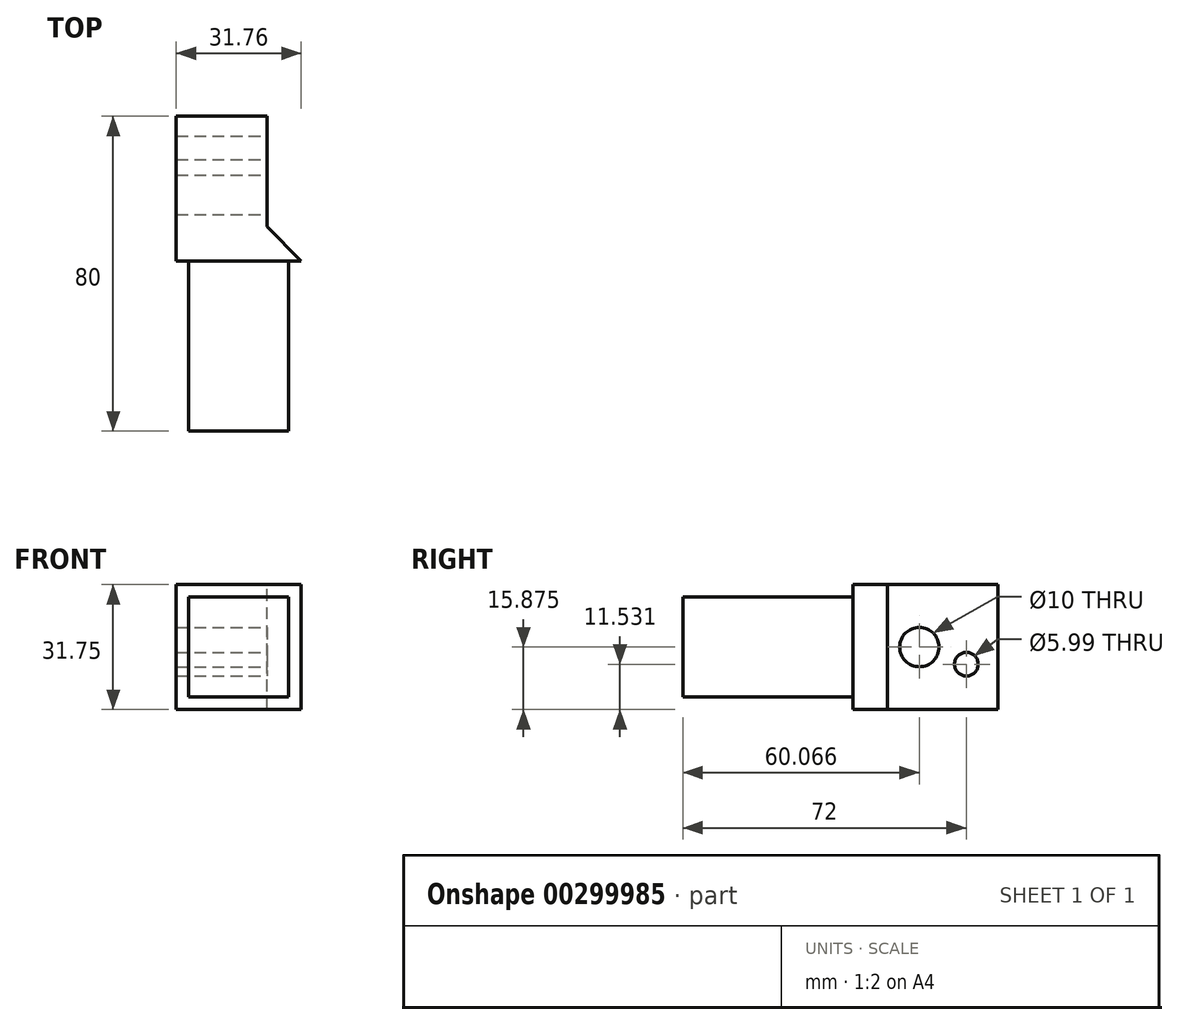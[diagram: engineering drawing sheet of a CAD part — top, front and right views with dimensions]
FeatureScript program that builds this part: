
annotation { "Feature Type Name" : "Feature", "Feature Type Description" : "" }
export const myFeature = defineFeature(function(context is Context, id is Id, definition is map)
    precondition{}
    {
        {
            var Q0;
            Q0=qCreatedBy(makeId("Top.planeOp"),FACE);
            var sketch = newSketch(context, id + "F0", { "sketchPlane" : qUnion([Q0])});
            skLineSegment(sketch, "E0.bottom", {"start": v(-15.88, 40) * mm, "end": v(15.88, 40) * mm});
            skLineSegment(sketch, "E0.top", {"start": v(-15.88, -40) * mm, "end": v(15.88, -40) * mm});
            skLineSegment(sketch, "E0.left", {"start": v(-15.88, 40) * mm, "end": v(-15.88, -40) * mm});
            skLineSegment(sketch, "E0.right", {"start": v(15.88, 40) * mm, "end": v(15.88, -40) * mm});
            skSolve(sketch);
        }
        {
            var Q0;
            Q0=qSketchRegion(id+"F0",true);
            extrude(context, id + "F1", {"entities" : qUnion([Q0]), "depth" : 31.75 * mm, "offsetDistance" : 25 * mm});
        }
        {
            var Q0;
            Q0=makeQuery(id+"F1.opExtrude","SWEPT_FACE",FACE,{"disambiguationData":[OSD([sQuery(id+"F0.wireOp",EDGE,"E0.right")])]});
            var sketch = newSketch(context, id + "F2", { "sketchPlane" : qUnion([Q0])});
            skCircle(sketch, "E1", {"center": v(20.07, 15.88) * mm, "radius": 5 * mm});
            skLineSegment(sketch, "E2", {"start": v(20.07, 15.88) * mm, "end": v(26.86, 15.88) * mm});
            skCircle(sketch, "E3", {"center": v(32, 11.53) * mm, "radius": 3 * mm});
            skLineSegment(sketch, "E4", {"start": v(32, 11.53) * mm, "end": v(20.07, 15.88) * mm});
            skSolve(sketch);
        }
        {
            var Q0;
            Q0=qSketchRegion(id+"F2",true);
            extrude(context, id + "F3", {"entities" : qUnion([Q0]), "operationType" : NewBodyOperationType.REMOVE, "endBound" : BoundingType.THROUGH_ALL, "oppositeDirection" : true, "depth" : 25 * mm, "offsetDistance" : 25 * mm});
        }
        {
            var Q0;
            Q0=makeQuery(id+"F1.opExtrude","CAP_FACE",FACE,{"disambiguationData":[OSD([sQuery(id+"F0.wireOp",EDGE,"E0.bottom"),sQuery(id+"F0.wireOp",EDGE,"E0.top"),sQuery(id+"F0.wireOp",EDGE,"E0.left"),sQuery(id+"F0.wireOp",EDGE,"E0.right")])],"isStart":false});
            var sketch = newSketch(context, id + "F4", { "sketchPlane" : qUnion([Q0])});
            skLineSegment(sketch, "E5", {"start": v(-12.7, -50) * mm, "end": v(-12.7, 10) * mm});
            skLineSegment(sketch, "E6", {"start": v(-12.7, 10) * mm, "end": v(12.7, 10) * mm});
            skLineSegment(sketch, "E7", {"start": v(12.7, 10) * mm, "end": v(12.7, -50) * mm});
            skLineSegment(sketch, "E8", {"start": v(12.7, -50) * mm, "end": v(-12.7, -50) * mm});
            skLineSegment(sketch, "E9", {"start": v(15.88, 40) * mm, "end": v(15.88, -63.27) * mm});
            skLineSegment(sketch, "E10", {"start": v(-12.7, 3.25) * mm, "end": v(-28.39, 3.25) * mm});
            skLineSegment(sketch, "E11", {"start": v(-28.39, 3.25) * mm, "end": v(29.3, 3.25) * mm});
            skLineSegment(sketch, "E12", {"start": v(29.3, 3.25) * mm, "end": v(29.3, -68.48) * mm});
            skLineSegment(sketch, "E13", {"start": v(29.3, -68.48) * mm, "end": v(-28.39, -68.48) * mm});
            skLineSegment(sketch, "E14", {"start": v(-28.39, -68.48) * mm, "end": v(-28.39, 3.25) * mm});
            skSolve(sketch);
        }
        {
            var Q0;
            {var subQ0=sQuery(id+"F4.wireOp",EDGE,"E8");Q0=makeQuery(id+"F4.imprint","IMPRINT",FACE,{"disambiguationData":[TD([[makeQuery(id+"F4.imprint","IMPRINT",EDGE,{"derivedFrom":subQ0}),-1.0]])]});}
            var Q1;
            {var subQ0=sQuery(id+"F4.wireOp",EDGE,"E11");var subQ1=sQuery(id+"F4.wireOp",EDGE,"E7");var subQ2=makeQuery(id+"F4.imprint","INTERSECT",VERTEX,{"derivedFrom":[subQ1,subQ0]});Q1=makeQuery(id+"F4.imprint","IMPRINT",FACE,{"disambiguationData":[TD([[makeQuery(id+"F4.imprint","IMPRINT",EDGE,{"disambiguationData":[TD([[subQ2,-1.0]])],"derivedFrom":subQ1}),1.0]])]});}
            var Q2;
            {var subQ0=sQuery(id+"F4.wireOp",EDGE,"E11");var subQ1=sQuery(id+"F4.wireOp",EDGE,"E5");var subQ2=makeQuery(id+"F4.imprint","INTERSECT",VERTEX,{"derivedFrom":[subQ1,subQ0]});Q2=makeQuery(id+"F4.imprint","IMPRINT",FACE,{"disambiguationData":[TD([[makeQuery(id+"F4.imprint","IMPRINT",EDGE,{"disambiguationData":[TD([[subQ2,1.0]])],"derivedFrom":subQ1}),1.0]])]});}
            extrude(context, id + "F5", {"entities" : qUnion([Q0, Q1, Q2]), "operationType" : NewBodyOperationType.REMOVE, "endBound" : BoundingType.THROUGH_ALL, "oppositeDirection" : true, "depth" : 25 * mm, "offsetDistance" : 25 * mm});
        }
        {
            var Q0;
            Q0=makeQuery(id+"F1.opExtrude","SWEPT_FACE",FACE,{"disambiguationData":[OSD([sQuery(id+"F0.wireOp",EDGE,"E0.right")])]});
            var sketch = newSketch(context, id + "F6", { "sketchPlane" : qUnion([Q0])});
            skLineSegment(sketch, "E15.bottom", {"start": v(3.25, 28.58) * mm, "end": v(-44.46, 28.57) * mm});
            skLineSegment(sketch, "E15.top", {"start": v(3.25, 40.72) * mm, "end": v(-44.46, 40.72) * mm});
            skLineSegment(sketch, "E15.left", {"start": v(3.25, 28.57) * mm, "end": v(3.25, 40.72) * mm});
            skLineSegment(sketch, "E15.right", {"start": v(-44.46, 28.57) * mm, "end": v(-44.46, 40.72) * mm});
            skLineSegment(sketch, "E16.bottom", {"start": v(3.25, 3.17) * mm, "end": v(-44.46, 3.17) * mm});
            skLineSegment(sketch, "E16.top", {"start": v(3.25, -7.24) * mm, "end": v(-44.46, -7.24) * mm});
            skLineSegment(sketch, "E16.left", {"start": v(3.25, 3.17) * mm, "end": v(3.25, -7.24) * mm});
            skLineSegment(sketch, "E16.right", {"start": v(-44.46, 3.17) * mm, "end": v(-44.46, -7.24) * mm});
            skSolve(sketch);
        }
        {
            var Q0;
            Q0=qSketchRegion(id+"F6",true);
            extrude(context, id + "F7", {"entities" : qUnion([Q0]), "operationType" : NewBodyOperationType.REMOVE, "endBound" : BoundingType.THROUGH_ALL, "oppositeDirection" : true, "depth" : 25 * mm, "offsetDistance" : 25 * mm});
        }
        {
            var Q0;
            Q0=makeQuery(id+"F1.opExtrude","CAP_FACE",FACE,{"disambiguationData":[OSD([sQuery(id+"F0.wireOp",EDGE,"E0.bottom"),sQuery(id+"F0.wireOp",EDGE,"E0.top"),sQuery(id+"F0.wireOp",EDGE,"E0.left"),sQuery(id+"F0.wireOp",EDGE,"E0.right")])],"isStart":false});
            var sketch = newSketch(context, id + "F8", { "sketchPlane" : qUnion([Q0])});
            skLineSegment(sketch, "E17.bottom", {"start": v(15.88, 40) * mm, "end": v(7.12, 40) * mm});
            skLineSegment(sketch, "E17.top", {"start": v(15.88, 3.25) * mm, "end": v(7.12, 3.25) * mm});
            skLineSegment(sketch, "E17.left", {"start": v(15.88, 40) * mm, "end": v(15.88, 3.25) * mm});
            skLineSegment(sketch, "E17.right", {"start": v(7.12, 40) * mm, "end": v(7.13, 3.25) * mm});
            skLineSegment(sketch, "E18", {"start": v(15.88, 3.25) * mm, "end": v(7.12, 12) * mm});
            skSolve(sketch);
        }
        {
            var Q0;
            {var subQ0=sQuery(id+"F8.wireOp",EDGE,"E17.bottom");Q0=makeQuery(id+"F8.imprint","IMPRINT",FACE,{"disambiguationData":[TD([[makeQuery(id+"F8.imprint","IMPRINT",EDGE,{"derivedFrom":subQ0}),-1.0]])]});}
            extrude(context, id + "F9", {"entities" : qUnion([Q0]), "operationType" : NewBodyOperationType.REMOVE, "endBound" : BoundingType.THROUGH_ALL, "oppositeDirection" : true, "depth" : 25.4 * mm, "offsetDistance" : 25.4 * mm});
        }
    });
